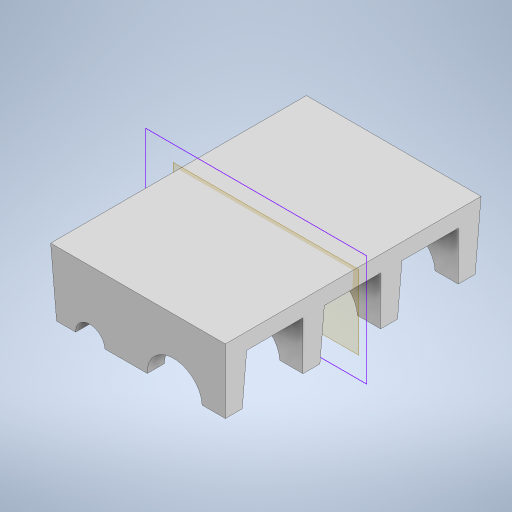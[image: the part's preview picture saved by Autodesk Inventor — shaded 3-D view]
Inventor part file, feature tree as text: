
AUTODESK INVENTOR PART (.ipt)
format: ipt  version: 2023 (Build 270158000, 158)  size: 296,960 bytes
history: native  units: in
note: dims shown in document units (in); Inventor stores cm internally (conversion verified against a paired STEP export)
features: extrude x2, sketch x2, plane x1, draft x1
ambient origin geometry x8: Origin, YZ Plane, XZ Plane, XY Plane, X Axis, Y Axis, Z Axis, Center Point
bodies: Solid1 (feature_tree)
feature tree (6):
  extrude  "Extrusion1"  Depth=5.0in
  extrude  "Extrusion2"  Depth=0.5in
  plane  "Work Plane1"
  sketch  "Sketch5"  dims[d3=7.4in d4=0.0in d15=1.4in d16=3.7in d17=6.0in d18=0.5in d20=2.528in d21=7.4in d22=0.0in d25=1.5in d26=0.866in d31=1.2546in d32=0.5669in d33=2.0in d34=1.5in d35=0.0172in d27=0.5in d28=0.0344in d29=0.0in d30=0.0in d36=0.5in d37=0.0344in d38=0.5in d39=0.0344in]
  draft  "FaceDraft1"
  sketch  "Sketch1"  dims[d0=5.0in d2=1.625in]
